# Revit family: _Camera-Security-Panasonic-360-degree-Vandal_Resistant-Outdoor-Dome-Network-X4573L
name_source: partatom
category: Security Devices
units: mm (PartAtom-declared; Revit-internal decimal feet)

## family parameters
Cut with Voids When Loaded = No
Host = Face
Maintain Annotation Orientation = No
OmniClass Number = 23.85.10.14.11
OmniClass Title = Cameras
Part Type = Normal
Room Calculation Point = No
Round Connector Dimension = Use Diameter
Shared = No

## types (4) — shared parameters
Alarm Input Or Output Specification = ALARM IN1 (Alarm input 1/ Auto time adjustment input) (x1), ALARM IN2 (Alarm input 2/ ALARM OUT) (x1), ALARM IN3 (Alarm input 3/ AUX OUT) (x1)
Angle Of View = 183
Audio In = 3.5 mm stereo mini jack
Audio Out = 3.5 mm stereo mini jack
Base Height = 1.417 "
Equipment Abbreviation = SC
Family Version = 1.0.0
Focal Length = 0.055 "
Has POE = Yes
Height_Offset5 = 1.447 "
IP Or Analog = IP
Indoor Or Outdoor = Outdoor
Manufacturer = Panasonic
Minimum Illumination = 0 lx
Model Disclaimer = Contact Panasonic for more information
Mounting Positions = Mount Dependent or Surface Mount
Operational Humidity = 10% to 100 % (no condensation)
Power Active = 12.5 W
Product Material = Paint - Panasonic - Sail White
Product Page URL = https://security.panasonic.com
Provide Feedback = https://www.surveymonkey.com
Regulatory Compliance = UL (UL60950-1), c-UL (CSA C22.2 No.60950-1), CE, IEC60950-1, FCC (Part15 ClassA), ICES003 ClassA, EN55022 ClassB, EN55024
Scanning Area H = 0.218 "
Scanning Area V = 0.218 "
Shock Resistance = 50J (IEC 60068-2-75 compliant), IK10 (IEC 62262)
Storage Temperature = -22 °F to 140 °F
URL = http://security.panasonic.com
Vandal Resistant = Yes
Voltage DC = 12 V
Water and Dust Resistance = IP66(IEC60529), Type 4X(UL50), NEMA 4X compliant
Wide Dynamic Range = Yes
z Camera Axis Const Length = 7.874 "
z Horizontal FOV = 183.00°
z Vertical FOV = 183.00°
zero-valued in all types: Default Elevation

## per-type parameters (varying)
| type | Communication Ports | Date Last Modified | Description | Part Description | Product Documentation Link |
| WV-X4571L | 10Base-T / 100Base-TX, RJ-45 | 2018/01/15 | Security Camera, H.264/H.265 360-degree, Vandal Resistant, Outdoor, Dome, 9 Megapixel, Network, X4571L | Security Camera, H.264/H.265 360-degree, Vandal Resistant, Outdoor, Dome, 9 Megapixel, Network, X4571L | http://ssbu-t.psn-web.net |
| WV-X4571LM | 10Base-T / 100Base-TX, M12 connector | 2018/01/15 | Security Camera, H.264/H.265 360-degree, Vandal Resistant, Outdoor, Dome, 9 Megapixel, Network, X4571LM | Security Camera, H.264/H.265 360-degree, Vandal Resistant, Outdoor, Dome, 9 Megapixel, Network, X4571LM | http://ssbu-t.psn-web.net |
| WV-X4573L | 10Base-T / 100Base-TX, RJ-45 | 2020/10/28 | Security Camera, H.264/H.265 360-degree, Vandal Resistant, Outdoor, Dome, 9 Megapixel, Network, X4573L | Security Camera, H.264/H.265 360-degree, Vandal Resistant, Outdoor, Dome, 9 Megapixel, Network, X4573L | https://bizpartner.panasonic.net |
| WV-X4573LM | 10Base-T / 100Base-TX, M12 connector | 2020/10/28 | Security Camera, H.264/H.265 360-degree, Vandal Resistant, Outdoor, Dome, 9 Megapixel, Network, X4573LM | Security Camera, H.264/H.265 360-degree, Vandal Resistant, Outdoor, Dome, 9 Megapixel, Network, X4573LM | https://bizpartner.panasonic.net |

note: column(s) folded — value = type name in every type: Model, Part Number

## geometry (parser evidence)
native form markers: Blend x2, Sweep x3
no freeform markers — native parametric forms only
